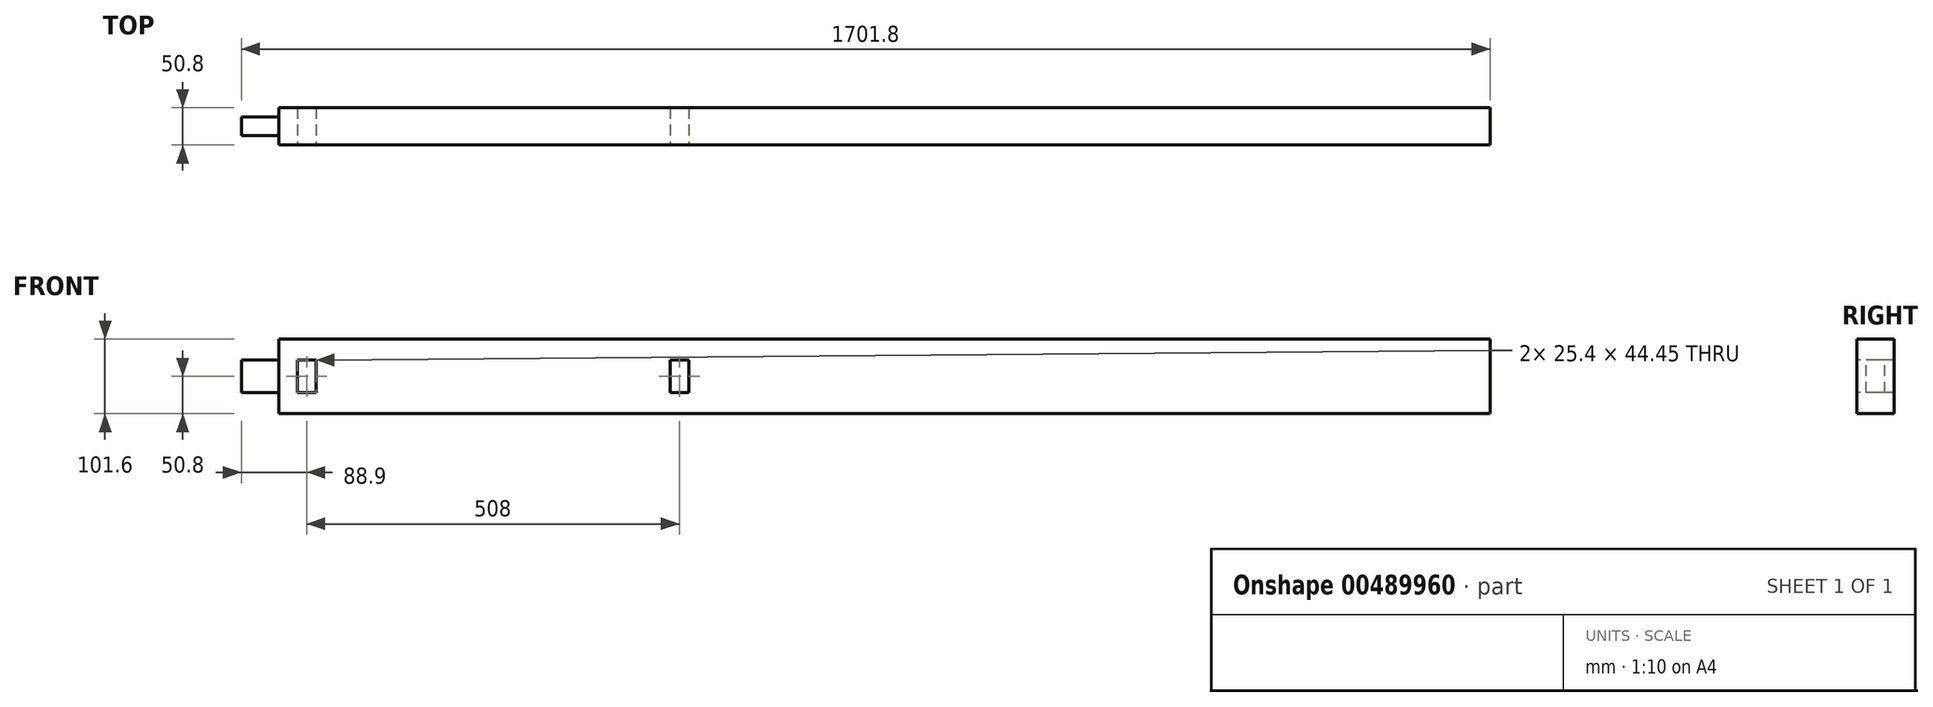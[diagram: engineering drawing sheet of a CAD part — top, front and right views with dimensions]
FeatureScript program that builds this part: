
annotation { "Feature Type Name" : "Feature", "Feature Type Description" : "" }
export const myFeature = defineFeature(function(context is Context, id is Id, definition is map)
    precondition{}
    {
        {
            var Q0;
            Q0=qCreatedBy(makeId("Right.planeOp"),FACE);
            var sketch = newSketch(context, id + "F0", { "sketchPlane" : qUnion([Q0])});
            skLineSegment(sketch, "E0.bottom", {"start": v(-25.4, -50.8) * mm, "end": v(25.4, -50.8) * mm});
            skLineSegment(sketch, "E0.top", {"start": v(-25.4, 50.8) * mm, "end": v(25.4, 50.8) * mm});
            skLineSegment(sketch, "E0.left", {"start": v(-25.4, -50.8) * mm, "end": v(-25.4, 50.8) * mm});
            skLineSegment(sketch, "E0.right", {"start": v(25.4, -50.8) * mm, "end": v(25.4, 50.8) * mm});
            skPoint(sketch, "E0.middle", {"position": v(0, 0) * mm});
            skSolve(sketch);
        }
        {
            var Q0;
            Q0 = qSketchRegion(id + "F0", true);
            extrude(context, id + "F1", {"entities" : qUnion([Q0]), "endBound" : BoundingType.SYMMETRIC, "depth" : 1701.8 * mm});
        }
        {
            var Q0;
            Q0=makeQuery(id+"F1.opExtrude","CAP_FACE",FACE,{"disambiguationData":[OSD([sQuery(id+"F0.wireOp",EDGE,"E0.bottom"),sQuery(id+"F0.wireOp",EDGE,"E0.top"),sQuery(id+"F0.wireOp",EDGE,"E0.left"),sQuery(id+"F0.wireOp",EDGE,"E0.right")])],"isStart":true});
            var sketch = newSketch(context, id + "F2", { "sketchPlane" : qUnion([Q0])});
            skLineSegment(sketch, "E1.bottom", {"start": v(-12.7, -22.23) * mm, "end": v(12.7, -22.23) * mm});
            skLineSegment(sketch, "E1.top", {"start": v(-12.7, 22.23) * mm, "end": v(12.7, 22.23) * mm});
            skLineSegment(sketch, "E1.left", {"start": v(-12.7, -22.23) * mm, "end": v(-12.7, 22.23) * mm});
            skLineSegment(sketch, "E1.right", {"start": v(12.7, -22.23) * mm, "end": v(12.7, 22.23) * mm});
            skPoint(sketch, "E1.middle", {"position": v(0, 0) * mm});
            skLineSegment(sketch, "E2.bottom", {"start": v(25.4, -50.8) * mm, "end": v(-25.4, -50.8) * mm});
            skLineSegment(sketch, "E2.top", {"start": v(25.4, 50.8) * mm, "end": v(-25.4, 50.8) * mm});
            skLineSegment(sketch, "E2.left", {"start": v(25.4, -50.8) * mm, "end": v(25.4, 50.8) * mm});
            skLineSegment(sketch, "E2.right", {"start": v(-25.4, -50.8) * mm, "end": v(-25.4, 50.8) * mm});
            skSolve(sketch);
        }
        {
            var Q0;
            Q0 = qSketchRegion(id + "F2", true);
            extrude(context, id + "F3", {"entities" : qUnion([Q0]), "operationType" : NewBodyOperationType.REMOVE, "oppositeDirection" : true, "depth" : 50.8 * mm});
        }
        {
            var Q0;
            Q0=makeQuery(id+"F1.opExtrude","SWEPT_FACE",FACE,{"disambiguationData":[OSD([sQuery(id+"F0.wireOp",EDGE,"E0.left")])]});
            var sketch = newSketch(context, id + "F4", { "sketchPlane" : qUnion([Q0])});
            skLineSegment(sketch, "E3.bottom", {"start": v(-774.7, 22.23) * mm, "end": v(-749.3, 22.23) * mm});
            skLineSegment(sketch, "E3.top", {"start": v(-774.7, -22.23) * mm, "end": v(-749.3, -22.23) * mm});
            skLineSegment(sketch, "E3.left", {"start": v(-774.7, 22.23) * mm, "end": v(-774.7, -22.23) * mm});
            skLineSegment(sketch, "E3.right", {"start": v(-749.3, 22.23) * mm, "end": v(-749.3, -22.23) * mm});
            skPoint(sketch, "E3.middle", {"position": v(-762, 0) * mm});
            skLineSegment(sketch, "E4.bottom", {"start": v(-266.7, -22.23) * mm, "end": v(-241.3, -22.23) * mm});
            skLineSegment(sketch, "E4.top", {"start": v(-266.7, 22.23) * mm, "end": v(-241.3, 22.23) * mm});
            skLineSegment(sketch, "E4.left", {"start": v(-266.7, -22.23) * mm, "end": v(-266.7, 22.23) * mm});
            skLineSegment(sketch, "E4.right", {"start": v(-241.3, -22.23) * mm, "end": v(-241.3, 22.23) * mm});
            skPoint(sketch, "E4.middle", {"position": v(-254, 0) * mm});
            skSolve(sketch);
        }
        {
            var Q0;
            Q0 = qSketchRegion(id + "F4", true);
            extrude(context, id + "F5", {"entities" : qUnion([Q0]), "operationType" : NewBodyOperationType.REMOVE, "endBound" : BoundingType.THROUGH_ALL, "oppositeDirection" : true, "depth" : 25.4 * mm});
        }
    });
